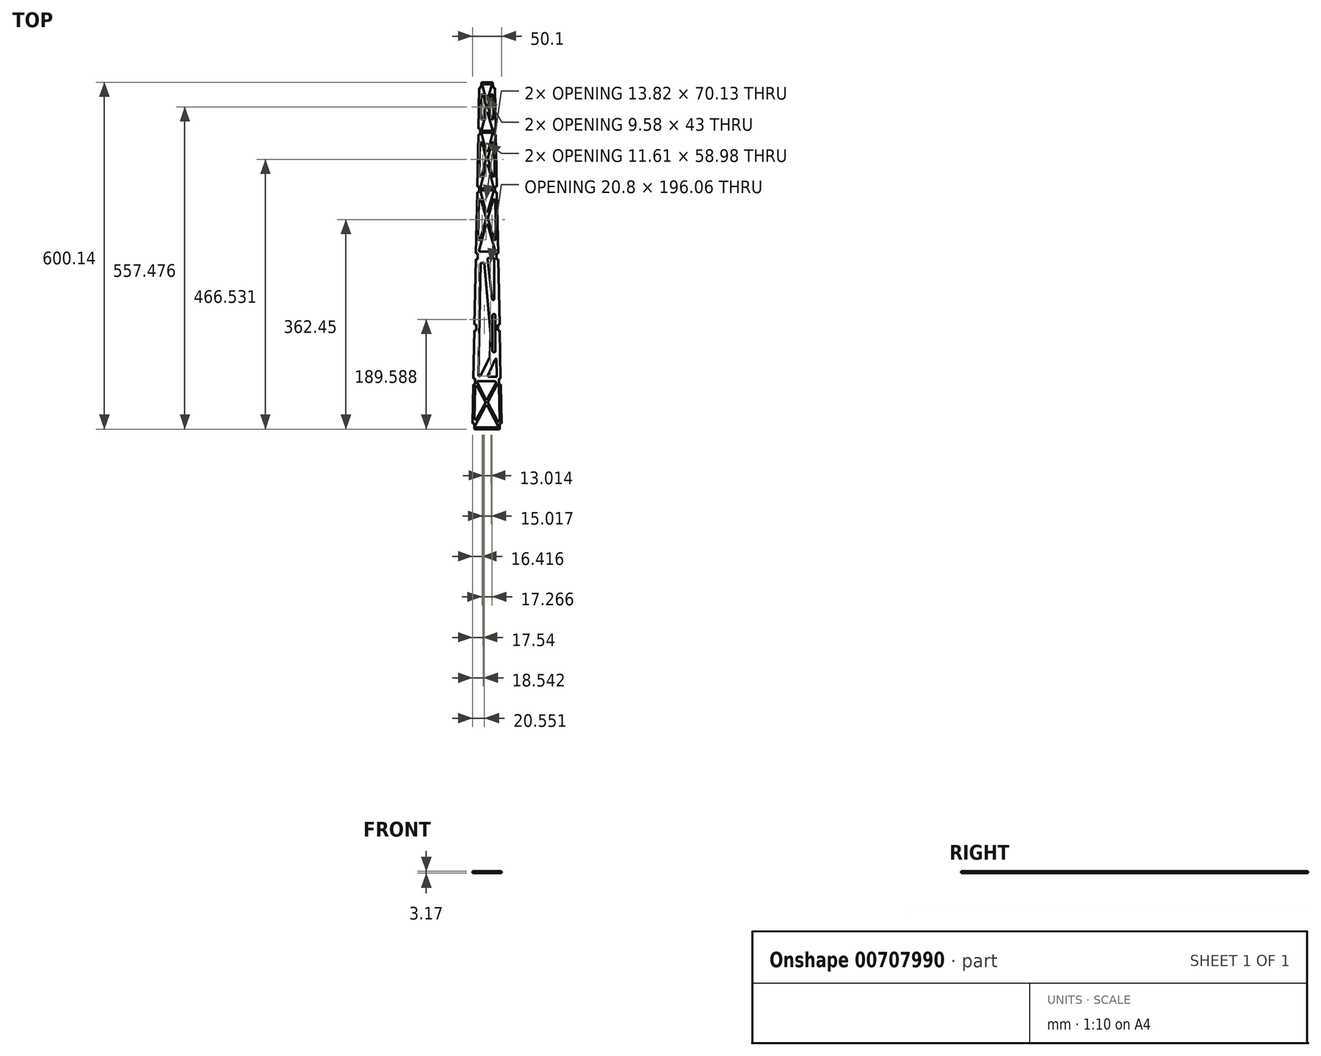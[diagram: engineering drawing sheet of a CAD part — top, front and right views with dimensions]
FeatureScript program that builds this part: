
annotation { "Feature Type Name" : "Feature", "Feature Type Description" : "" }
export const myFeature = defineFeature(function(context is Context, id is Id, definition is map)
    precondition{}
    {
        {
            var Q0;
            Q0=qCreatedBy(makeId("Top.planeOp"), FACE);
            var sketch = newSketch(context, id + "F0", { "sketchPlane" : qUnion([Q0])});
            skLineSegment(sketch, "E0.0.0", {"start": v(-3.6, 283.5) * mm, "end": v(-13.63, 283.5) * mm});
            skLineSegment(sketch, "E1", {"start": v(-14.7, -223.96) * mm, "end": v(1.24, -191.58) * mm});
            skArc(sketch, "E2.filletArc", {"start": v(-18.49, -223.03) * mm, "mid": v(-16.97, -225.02) * mm, "end": v(-14.7, -223.96) * mm});
            skLineSegment(sketch, "E3", {"start": v(1.24, -191.58) * mm, "end": v(2.31, -152.2) * mm});
            skLineSegment(sketch, "E4", {"start": v(2.31, -152.2) * mm, "end": v(-8.41, -29.18) * mm});
            skLineSegment(sketch, "E5.0", {"start": v(18.18, -301.3) * mm, "end": v(17, -241.76) * mm});
            skLineSegment(sketch, "E5.1", {"start": v(11.95, 12.78) * mm, "end": v(10.6, 78.94) * mm});
            skLineSegment(sketch, "E5.2", {"start": v(2.26, 280.33) * mm, "end": v(-9.44, 280.33) * mm});
            skLineSegment(sketch, "E6.0", {"start": v(-14.1, 260.4) * mm, "end": v(-14.89, 221.37) * mm});
            skLineSegment(sketch, "E6.1", {"start": v(-24.24, -244.27) * mm, "end": v(-25.3, -298.14) * mm});
            skLineSegment(sketch, "E6.2", {"start": v(-22.26, -313.46) * mm, "end": v(13.43, -313.46) * mm});
            skLineSegment(sketch, "E7", {"start": v(10.03, -233.97) * mm, "end": v(-18.8, -233.4) * mm});
            skLineSegment(sketch, "E8", {"start": v(8.13, -9.62) * mm, "end": v(-15.31, -9.62) * mm});
            skLineSegment(sketch, "E9", {"start": v(13.25, -240.86) * mm, "end": v(-2.04, -269.42) * mm});
            skLineSegment(sketch, "E10.0", {"start": v(14.42, -302.27) * mm, "end": v(-2.04, -271.3) * mm});
            skLineSegment(sketch, "E11.0", {"start": v(15.2, -310.52) * mm, "end": v(-2.59, -277.05) * mm});
            skLineSegment(sketch, "E12.0", {"start": v(11.75, -236.92) * mm, "end": v(-2.57, -263.67) * mm});
            skLineSegment(sketch, "E13.0", {"start": v(8.02, 12.2) * mm, "end": v(-1.8, 47.72) * mm});
            skLineSegment(sketch, "E14.0", {"start": v(10.06, -7.1) * mm, "end": v(-1.66, 35.3) * mm});
            skLineSegment(sketch, "E15.0", {"start": v(7.42, 94.07) * mm, "end": v(-1.66, 61.2) * mm});
            skLineSegment(sketch, "E16.0", {"start": v(6.68, 79.43) * mm, "end": v(-1.8, 48.78) * mm});
            skLineSegment(sketch, "E17.0", {"start": v(5.78, 121.9) * mm, "end": v(-1.82, 151.59) * mm});
            skLineSegment(sketch, "E18.0", {"start": v(7.53, 102.28) * mm, "end": v(-1.65, 138.11) * mm});
            skLineSegment(sketch, "E19.0", {"start": v(-12.97, 121.9) * mm, "end": v(-5.36, 151.59) * mm});
            skLineSegment(sketch, "E20.0", {"start": v(3.78, 220.81) * mm, "end": v(-1.8, 241.82) * mm});
            skLineSegment(sketch, "E21.MirrorCS", {"start": v(5.45, 202.15) * mm, "end": v(-1.66, 228.88) * mm});
            skLineSegment(sketch, "E22.0", {"start": v(4.2, 277.82) * mm, "end": v(-1.66, 255.8) * mm});
            skLineSegment(sketch, "E23.MirrorCS", {"start": v(2.98, 260.87) * mm, "end": v(-1.8, 242.85) * mm});
            skLineSegment(sketch, "E24.trimOffspring", {"start": v(-5.37, 241.82) * mm, "end": v(-10.96, 220.81) * mm});
            skLineSegment(sketch, "E25.trimOffspring", {"start": v(-5.52, 255.8) * mm, "end": v(-11.38, 277.82) * mm});
            skLineSegment(sketch, "E26.trimOffspring", {"start": v(-5.37, 242.85) * mm, "end": v(-10.16, 260.87) * mm});
            skLineSegment(sketch, "E27.trimOffspring", {"start": v(-5.52, 228.88) * mm, "end": v(-12.63, 202.15) * mm});
            skLineSegment(sketch, "E28.trimOffspring", {"start": v(-5.36, 152.58) * mm, "end": v(-11.85, 177.9) * mm});
            skLineSegment(sketch, "E29.trimOffspring", {"start": v(-1.82, 152.58) * mm, "end": v(4.66, 177.9) * mm});
            skLineSegment(sketch, "E30.trimOffspring", {"start": v(-5.53, 166.05) * mm, "end": v(-12.68, 193.96) * mm});
            skLineSegment(sketch, "E31.trimOffspring", {"start": v(-1.65, 166.05) * mm, "end": v(5.5, 193.96) * mm});
            skLineSegment(sketch, "E32.trimOffspring", {"start": v(-5.39, 48.78) * mm, "end": v(-13.86, 79.43) * mm});
            skLineSegment(sketch, "E33.trimOffspring", {"start": v(-5.52, 35.3) * mm, "end": v(-17.24, -7.1) * mm});
            skLineSegment(sketch, "E34.trimOffspring", {"start": v(-5.52, 61.2) * mm, "end": v(-14.6, 94.07) * mm});
            skLineSegment(sketch, "E35.trimOffspring", {"start": v(-5.39, 47.72) * mm, "end": v(-15.2, 12.2) * mm});
            skLineSegment(sketch, "E36.trimOffspring", {"start": v(-6.64, -269.41) * mm, "end": v(-20.48, -243.37) * mm});
            skLineSegment(sketch, "E37.trimOffspring", {"start": v(-6.65, -271.3) * mm, "end": v(-21.54, -299.12) * mm});
            skLineSegment(sketch, "E38.trimOffspring", {"start": v(-6.1, -263.66) * mm, "end": v(-20.6, -236.34) * mm});
            skLineSegment(sketch, "E39.trimOffspring", {"start": v(-6.12, -277.04) * mm, "end": v(-24.03, -310.51) * mm});
            skLineSegment(sketch, "E40.trimOffspring", {"start": v(9.72, 122.43) * mm, "end": v(8.6, 177.45) * mm});
            skLineSegment(sketch, "E41.trimOffspring", {"start": v(-17.79, 78.94) * mm, "end": v(-19.13, 12.78) * mm});
            skLineSegment(sketch, "E42.trimOffspring", {"start": v(-15.78, 177.45) * mm, "end": v(-16.9, 122.43) * mm});
            skLineSegment(sketch, "E43.trimOffspring", {"start": v(7.7, 221.37) * mm, "end": v(6.91, 260.4) * mm});
            skLineSegment(sketch, "E44", {"start": v(10.22, -197.1) * mm, "end": v(-1.88, -223.48) * mm});
            skLineSegment(sketch, "E45", {"start": v(-0.06, -226.3) * mm, "end": v(11.28, -226.3) * mm});
            skLineSegment(sketch, "E46", {"start": v(13.28, -224.27) * mm, "end": v(12.72, -195.53) * mm});
            skLineSegment(sketch, "E47", {"start": v(11.16, -195.18) * mm, "end": v(10.22, -197.1) * mm});
            skLineSegment(sketch, "E48", {"start": v(6.99, -20.51) * mm, "end": v(-0.88, -20.67) * mm});
            skLineSegment(sketch, "E49", {"start": v(-2.83, -22.9) * mm, "end": v(5.04, -91.54) * mm});
            skLineSegment(sketch, "E50", {"start": v(9.03, -91.32) * mm, "end": v(9.03, -22.51) * mm});
            skPoint(sketch, "E51.visualSharp", {"position": v(16.76, -313.46) * mm});
            skArc(sketch, "E51.filletArc", {"start": v(13.43, -313.46) * mm, "mid": v(15.14, -312.49) * mm, "end": v(15.2, -310.52) * mm});
            skArc(sketch, "E52.filletArc", {"start": v(14.42, -302.27) * mm, "mid": v(16.68, -303.27) * mm, "end": v(18.18, -301.3) * mm});
            skArc(sketch, "E53.filletArc", {"start": v(17, -241.76) * mm, "mid": v(15.48, -239.86) * mm, "end": v(13.25, -240.86) * mm});
            skArc(sketch, "E54.filletArc", {"start": v(-20.48, -243.37) * mm, "mid": v(-22.7, -242.37) * mm, "end": v(-24.24, -244.27) * mm});
            skArc(sketch, "E55.filletArc", {"start": v(-25.3, -298.14) * mm, "mid": v(-23.8, -300.11) * mm, "end": v(-21.54, -299.12) * mm});
            skArc(sketch, "E56.filletArc", {"start": v(-24.03, -310.51) * mm, "mid": v(-23.98, -312.49) * mm, "end": v(-22.26, -313.46) * mm});
            skPoint(sketch, "E57.visualSharp", {"position": v(-22.2, -233.34) * mm});
            skArc(sketch, "E57.filletArc", {"start": v(-18.8, -233.4) * mm, "mid": v(-20.55, -234.36) * mm, "end": v(-20.6, -236.34) * mm});
            skPoint(sketch, "E58.visualSharp", {"position": v(13.29, -234.04) * mm});
            skArc(sketch, "E58.filletArc", {"start": v(11.75, -236.92) * mm, "mid": v(11.71, -234.96) * mm, "end": v(10.03, -233.97) * mm});
            skPoint(sketch, "E59.visualSharp", {"position": v(-4.34, -266.98) * mm});
            skArc(sketch, "E59.filletArc", {"start": v(-6.1, -263.66) * mm, "mid": v(-4.33, -264.72) * mm, "end": v(-2.57, -263.67) * mm});
            skPoint(sketch, "E60.visualSharp", {"position": v(-6.14, -270.35) * mm});
            skArc(sketch, "E60.filletArc", {"start": v(-6.65, -271.3) * mm, "mid": v(-6.4, -270.35) * mm, "end": v(-6.64, -269.41) * mm});
            skPoint(sketch, "E61.visualSharp", {"position": v(-4.35, -273.73) * mm});
            skArc(sketch, "E61.filletArc", {"start": v(-2.59, -277.05) * mm, "mid": v(-4.35, -275.99) * mm, "end": v(-6.12, -277.04) * mm});
            skPoint(sketch, "E62.visualSharp", {"position": v(-2.54, -270.36) * mm});
            skArc(sketch, "E62.filletArc", {"start": v(-2.04, -269.42) * mm, "mid": v(-2.27, -270.36) * mm, "end": v(-2.04, -271.3) * mm});
            skPoint(sketch, "E63.visualSharp", {"position": v(-3.18, -226.3) * mm});
            skArc(sketch, "E63.filletArc", {"start": v(-1.88, -223.48) * mm, "mid": v(-1.75, -225.39) * mm, "end": v(-0.06, -226.3) * mm});
            skPoint(sketch, "E64.visualSharp", {"position": v(13.32, -226.3) * mm});
            skArc(sketch, "E64.filletArc", {"start": v(11.28, -226.3) * mm, "mid": v(12.7, -225.71) * mm, "end": v(13.28, -224.27) * mm});
            skPoint(sketch, "E65.visualSharp", {"position": v(12.65, -192.14) * mm});
            skArc(sketch, "E65.filletArc", {"start": v(12.72, -195.53) * mm, "mid": v(12.07, -194.74) * mm, "end": v(11.16, -195.18) * mm});
            skPoint(sketch, "E66.visualSharp", {"position": v(9.03, -126.31) * mm});
            skPoint(sketch, "E67.visualSharp", {"position": v(9.03, -20.47) * mm});
            skArc(sketch, "E67.filletArc", {"start": v(9.03, -22.51) * mm, "mid": v(8.43, -21.09) * mm, "end": v(6.99, -20.51) * mm});
            skPoint(sketch, "E68.visualSharp", {"position": v(-3.08, -20.72) * mm});
            skArc(sketch, "E68.filletArc", {"start": v(-0.88, -20.67) * mm, "mid": v(-2.35, -21.36) * mm, "end": v(-2.83, -22.9) * mm});
            skArc(sketch, "E69.filletArc", {"start": v(8.02, 12.2) * mm, "mid": v(10.24, 10.76) * mm, "end": v(11.95, 12.78) * mm});
            skPoint(sketch, "E70.visualSharp", {"position": v(10.76, -9.62) * mm});
            skArc(sketch, "E70.filletArc", {"start": v(8.13, -9.62) * mm, "mid": v(9.72, -8.83) * mm, "end": v(10.06, -7.1) * mm});
            skPoint(sketch, "E71.visualSharp", {"position": v(-17.94, -9.62) * mm});
            skArc(sketch, "E71.filletArc", {"start": v(-17.24, -7.1) * mm, "mid": v(-16.9, -8.83) * mm, "end": v(-15.31, -9.62) * mm});
            skArc(sketch, "E72.filletArc", {"start": v(-19.13, 12.78) * mm, "mid": v(-17.42, 10.76) * mm, "end": v(-15.2, 12.2) * mm});
            skArc(sketch, "E73.filletArc", {"start": v(-13.86, 79.43) * mm, "mid": v(-16.04, 80.89) * mm, "end": v(-17.79, 78.94) * mm});
            skPoint(sketch, "E74.visualSharp", {"position": v(-3.6, 54.22) * mm});
            skArc(sketch, "E74.filletArc", {"start": v(-5.52, 61.2) * mm, "mid": v(-3.6, 59.73) * mm, "end": v(-1.66, 61.2) * mm});
            skPoint(sketch, "E75.visualSharp", {"position": v(-1.94, 48.25) * mm});
            skArc(sketch, "E75.filletArc", {"start": v(-1.8, 48.78) * mm, "mid": v(-1.87, 48.25) * mm, "end": v(-1.8, 47.72) * mm});
            skPoint(sketch, "E76.visualSharp", {"position": v(-3.6, 42.28) * mm});
            skArc(sketch, "E76.filletArc", {"start": v(-1.66, 35.3) * mm, "mid": v(-3.6, 36.78) * mm, "end": v(-5.52, 35.3) * mm});
            skPoint(sketch, "E77.visualSharp", {"position": v(-5.24, 48.25) * mm});
            skArc(sketch, "E77.filletArc", {"start": v(-5.39, 47.72) * mm, "mid": v(-5.32, 48.25) * mm, "end": v(-5.39, 48.78) * mm});
            skArc(sketch, "E78.filletArc", {"start": v(10.6, 78.94) * mm, "mid": v(8.85, 80.89) * mm, "end": v(6.68, 79.43) * mm});
            skLineSegment(sketch, "E79.0", {"start": v(5.59, 99.78) * mm, "end": v(-12.77, 99.78) * mm});
            skLineSegment(sketch, "E80.MirrorCS", {"start": v(5.5, 96.6) * mm, "end": v(-12.68, 96.6) * mm});
            skLineSegment(sketch, "E81.0", {"start": v(3.51, 199.63) * mm, "end": v(-10.7, 199.63) * mm});
            skLineSegment(sketch, "E82.MirrorCS", {"start": v(3.56, 196.45) * mm, "end": v(-10.74, 196.45) * mm});
            skLineSegment(sketch, "E83.trimOffspring", {"start": v(-14.7, 102.28) * mm, "end": v(-5.53, 138.11) * mm});
            skArc(sketch, "E84.filletArc", {"start": v(7.42, 94.07) * mm, "mid": v(7.09, 95.81) * mm, "end": v(5.5, 96.6) * mm});
            skArc(sketch, "E85.filletArc", {"start": v(-12.68, 96.6) * mm, "mid": v(-14.27, 95.81) * mm, "end": v(-14.6, 94.07) * mm});
            skArc(sketch, "E86.filletArc", {"start": v(-14.7, 102.28) * mm, "mid": v(-14.35, 100.56) * mm, "end": v(-12.77, 99.78) * mm});
            skArc(sketch, "E87.filletArc", {"start": v(5.59, 99.78) * mm, "mid": v(7.17, 100.56) * mm, "end": v(7.53, 102.28) * mm});
            skArc(sketch, "E88.filletArc", {"start": v(5.78, 121.9) * mm, "mid": v(8, 120.4) * mm, "end": v(9.72, 122.43) * mm});
            skArc(sketch, "E89.filletArc", {"start": v(-16.9, 122.43) * mm, "mid": v(-15.17, 120.4) * mm, "end": v(-12.97, 121.9) * mm});
            skArc(sketch, "E90.filletArc", {"start": v(5.5, 193.96) * mm, "mid": v(5.14, 195.68) * mm, "end": v(3.56, 196.45) * mm});
            skArc(sketch, "E91.filletArc", {"start": v(3.51, 199.63) * mm, "mid": v(5.1, 200.41) * mm, "end": v(5.45, 202.15) * mm});
            skArc(sketch, "E92.filletArc", {"start": v(-12.63, 202.15) * mm, "mid": v(-12.28, 200.41) * mm, "end": v(-10.7, 199.63) * mm});
            skArc(sketch, "E93.filletArc", {"start": v(-10.74, 196.45) * mm, "mid": v(-12.32, 195.68) * mm, "end": v(-12.68, 193.96) * mm});
            skPoint(sketch, "E94.visualSharp", {"position": v(-3.6, 236.15) * mm});
            skArc(sketch, "E94.filletArc", {"start": v(-1.66, 228.88) * mm, "mid": v(-3.6, 230.36) * mm, "end": v(-5.52, 228.88) * mm});
            skPoint(sketch, "E95.visualSharp", {"position": v(-3.6, 158.5) * mm});
            skArc(sketch, "E95.filletArc", {"start": v(-5.53, 166.05) * mm, "mid": v(-3.6, 164.55) * mm, "end": v(-1.65, 166.05) * mm});
            skPoint(sketch, "E96.visualSharp", {"position": v(-3.6, 248.53) * mm});
            skArc(sketch, "E96.filletArc", {"start": v(-5.52, 255.8) * mm, "mid": v(-3.6, 254.31) * mm, "end": v(-1.66, 255.8) * mm});
            skPoint(sketch, "E97.visualSharp", {"position": v(-12.05, 280.33) * mm});
            skArc(sketch, "E97.filletArc", {"start": v(-9.44, 280.33) * mm, "mid": v(-11.03, 279.55) * mm, "end": v(-11.38, 277.82) * mm});
            skArc(sketch, "E98.filletArc", {"start": v(4.2, 277.82) * mm, "mid": v(3.85, 279.55) * mm, "end": v(2.26, 280.33) * mm});
            skPoint(sketch, "E99.visualSharp", {"position": v(-5.24, 242.34) * mm});
            skArc(sketch, "E99.filletArc", {"start": v(-5.37, 241.82) * mm, "mid": v(-5.3, 242.34) * mm, "end": v(-5.37, 242.85) * mm});
            skPoint(sketch, "E100.visualSharp", {"position": v(-1.95, 242.34) * mm});
            skArc(sketch, "E100.filletArc", {"start": v(-1.8, 242.85) * mm, "mid": v(-1.88, 242.34) * mm, "end": v(-1.8, 241.82) * mm});
            skArc(sketch, "E101.filletArc", {"start": v(8.6, 177.45) * mm, "mid": v(6.83, 179.4) * mm, "end": v(4.66, 177.9) * mm});
            skArc(sketch, "E102.filletArc", {"start": v(-11.85, 177.9) * mm, "mid": v(-14.01, 179.4) * mm, "end": v(-15.78, 177.45) * mm});
            skArc(sketch, "E103.filletArc", {"start": v(-14.89, 221.37) * mm, "mid": v(-13.17, 219.35) * mm, "end": v(-10.96, 220.81) * mm});
            skArc(sketch, "E104.filletArc", {"start": v(-10.16, 260.87) * mm, "mid": v(-12.34, 262.35) * mm, "end": v(-14.1, 260.4) * mm});
            skArc(sketch, "E105.filletArc", {"start": v(6.91, 260.4) * mm, "mid": v(5.15, 262.35) * mm, "end": v(2.98, 260.87) * mm});
            skArc(sketch, "E106.filletArc", {"start": v(3.78, 220.81) * mm, "mid": v(5.99, 219.35) * mm, "end": v(7.7, 221.37) * mm});
            skPoint(sketch, "E107.visualSharp", {"position": v(-3.6, 145.68) * mm});
            skArc(sketch, "E107.filletArc", {"start": v(-1.65, 138.11) * mm, "mid": v(-3.6, 139.62) * mm, "end": v(-5.53, 138.11) * mm});
            skPoint(sketch, "E108.visualSharp", {"position": v(-5.23, 152.08) * mm});
            skArc(sketch, "E108.filletArc", {"start": v(-5.36, 151.59) * mm, "mid": v(-5.3, 152.08) * mm, "end": v(-5.36, 152.58) * mm});
            skPoint(sketch, "E109.visualSharp", {"position": v(-1.95, 152.08) * mm});
            skArc(sketch, "E109.filletArc", {"start": v(-1.82, 152.58) * mm, "mid": v(-1.89, 152.08) * mm, "end": v(-1.82, 151.59) * mm});
            skArc(sketch, "E110.filletArc", {"start": v(5.04, -91.54) * mm, "mid": v(7.14, -93.31) * mm, "end": v(9.03, -91.32) * mm});
            skLineSegment(sketch, "E111", {"start": v(-18.49, -223.03) * mm, "end": v(-14.63, -29.01) * mm});
            skLineSegment(sketch, "E112", {"start": v(8.43, -120.01) * mm, "end": v(8.43, -181.2) * mm, "construction": true});
            skArc(sketch, "E113.0.startCap", {"start": v(5.93, -120.01) * mm, "mid": v(8.43, -117.51) * mm, "end": v(10.93, -120.01) * mm});
            skArc(sketch, "E113.0.endCap", {"start": v(10.93, -181.2) * mm, "mid": v(8.43, -183.7) * mm, "end": v(5.93, -181.2) * mm});
            skLineSegment(sketch, "E113.0.left", {"start": v(10.93, -120.01) * mm, "end": v(10.93, -181.2) * mm});
            skLineSegment(sketch, "E113.0.right", {"start": v(5.93, -120.01) * mm, "end": v(5.93, -181.2) * mm});
            skLineSegment(sketch, "E114.bottom", {"start": v(-27.12, -229.08) * mm, "end": v(-23.94, -229.14) * mm});
            skLineSegment(sketch, "E114.top", {"start": v(-27.31, -239.08) * mm, "end": v(-24.14, -239.14) * mm});
            skLineSegment(sketch, "E114.right", {"start": v(-23.94, -229.14) * mm, "end": v(-24.14, -239.14) * mm});
            skLineSegment(sketch, "E115", {"start": v(-4.39, -233.69) * mm, "end": v(-4.71, -315.99) * mm, "construction": true});
            skLineSegment(sketch, "E116.bottom", {"start": v(-25.28, -135.92) * mm, "end": v(-22.11, -135.98) * mm});
            skLineSegment(sketch, "E116.top", {"start": v(-25.48, -145.92) * mm, "end": v(-22.3, -145.98) * mm});
            skLineSegment(sketch, "E117.trimOffspring", {"start": v(-25.48, -145.92) * mm, "end": v(-27.12, -229.08) * mm});
            skLineSegment(sketch, "E118.bottom", {"start": v(-22.83, -12.78) * mm, "end": v(-19.66, -12.84) * mm});
            skLineSegment(sketch, "E118.top", {"start": v(-23.03, -22.78) * mm, "end": v(-19.86, -22.84) * mm});
            skLineSegment(sketch, "E118.right", {"start": v(-19.66, -12.84) * mm, "end": v(-19.86, -22.84) * mm});
            skLineSegment(sketch, "E119.bottom", {"start": v(-20.47, 103.2) * mm, "end": v(-17.3, 103.14) * mm});
            skLineSegment(sketch, "E119.top", {"start": v(-20.67, 93.2) * mm, "end": v(-17.5, 93.14) * mm});
            skLineSegment(sketch, "E119.right", {"start": v(-17.3, 103.14) * mm, "end": v(-17.5, 93.14) * mm});
            skLineSegment(sketch, "E120.trimOffspring", {"start": v(-20.67, 93.2) * mm, "end": v(-22.83, -12.78) * mm});
            skLineSegment(sketch, "E121.bottom", {"start": v(-18.44, 203.35) * mm, "end": v(-15.26, 203.29) * mm});
            skLineSegment(sketch, "E121.top", {"start": v(-18.64, 193.35) * mm, "end": v(-15.46, 193.3) * mm});
            skLineSegment(sketch, "E121.right", {"start": v(-15.26, 203.29) * mm, "end": v(-15.46, 193.3) * mm});
            skLineSegment(sketch, "E122.trimOffspring", {"start": v(-18.64, 193.35) * mm, "end": v(-20.47, 103.2) * mm});
            skLineSegment(sketch, "E123.top", {"start": v(-17, 273.51) * mm, "end": v(-13.82, 273.45) * mm});
            skLineSegment(sketch, "E124", {"start": v(-17, 273.51) * mm, "end": v(-18.44, 203.35) * mm});
            skLineSegment(sketch, "E125", {"start": v(-25.67, -316.63) * mm, "end": v(-4.71, -316.63) * mm});
            skLineSegment(sketch, "E126", {"start": v(-4.71, -315.99) * mm, "end": v(-4.71, -321.59) * mm, "construction": true});
            skLineSegment(sketch, "E127", {"start": v(-3.6, 283.5) * mm, "end": v(-3.6, 292.07) * mm, "construction": true});
            skLineSegment(sketch, "E128", {"start": v(-23.03, -22.78) * mm, "end": v(-25.28, -135.92) * mm});
            skLineSegment(sketch, "E129", {"start": v(-25.47, -306.6) * mm, "end": v(-25.67, -316.63) * mm});
            skLineSegment(sketch, "E130.MirrorCS", {"start": v(-3.6, 283.5) * mm, "end": v(6.44, 283.5) * mm});
            skLineSegment(sketch, "E131.MirrorCS", {"start": v(9.82, 273.51) * mm, "end": v(6.64, 273.45) * mm});
            skLineSegment(sketch, "E132.MirrorCS", {"start": v(9.82, 273.51) * mm, "end": v(11.26, 203.35) * mm});
            skLineSegment(sketch, "E133.MirrorCS", {"start": v(11.26, 203.35) * mm, "end": v(8.08, 203.29) * mm});
            skLineSegment(sketch, "E134.MirrorCS", {"start": v(8.08, 203.29) * mm, "end": v(8.28, 193.3) * mm});
            skLineSegment(sketch, "E135.MirrorCS", {"start": v(11.45, 193.35) * mm, "end": v(8.28, 193.3) * mm});
            skLineSegment(sketch, "E136.MirrorCS", {"start": v(11.45, 193.35) * mm, "end": v(13.29, 103.2) * mm});
            skLineSegment(sketch, "E137.MirrorCS", {"start": v(13.29, 103.2) * mm, "end": v(10.12, 103.14) * mm});
            skLineSegment(sketch, "E138.MirrorCS", {"start": v(10.12, 103.14) * mm, "end": v(10.32, 93.14) * mm});
            skLineSegment(sketch, "E139.MirrorCS", {"start": v(13.5, 93.2) * mm, "end": v(10.32, 93.14) * mm});
            skLineSegment(sketch, "E140.MirrorCS", {"start": v(13.5, 93.2) * mm, "end": v(15.65, -12.78) * mm});
            skLineSegment(sketch, "E141.MirrorCS", {"start": v(15.65, -12.78) * mm, "end": v(12.48, -12.84) * mm});
            skLineSegment(sketch, "E142.MirrorCS", {"start": v(12.48, -12.84) * mm, "end": v(12.68, -22.84) * mm});
            skLineSegment(sketch, "E143.MirrorCS", {"start": v(15.85, -22.78) * mm, "end": v(12.68, -22.84) * mm});
            skLineSegment(sketch, "E144.MirrorCS", {"start": v(15.85, -22.78) * mm, "end": v(18.1, -135.92) * mm});
            skLineSegment(sketch, "E145.MirrorCS", {"start": v(18.1, -135.92) * mm, "end": v(14.93, -135.98) * mm});
            skLineSegment(sketch, "E146.MirrorCS", {"start": v(18.3, -145.92) * mm, "end": v(15.12, -145.98) * mm});
            skLineSegment(sketch, "E147.MirrorCS", {"start": v(18.3, -145.92) * mm, "end": v(19.94, -229.08) * mm});
            skLineSegment(sketch, "E148.MirrorCS", {"start": v(19.94, -229.08) * mm, "end": v(16.76, -229.14) * mm});
            skLineSegment(sketch, "E149.MirrorCS", {"start": v(16.76, -229.14) * mm, "end": v(16.96, -239.14) * mm});
            skLineSegment(sketch, "E150.MirrorCS", {"start": v(20.13, -239.08) * mm, "end": v(16.96, -239.14) * mm});
            skLineSegment(sketch, "E151.MirrorCS", {"start": v(20.13, -239.08) * mm, "end": v(21.46, -306.54) * mm});
            skLineSegment(sketch, "E152.MirrorCS", {"start": v(18.29, -306.6) * mm, "end": v(21.46, -306.54) * mm});
            skLineSegment(sketch, "E153.MirrorCS", {"start": v(18.29, -306.6) * mm, "end": v(18.48, -316.63) * mm});
            skLineSegment(sketch, "E154", {"start": v(-4.71, -316.63) * mm, "end": v(18.48, -316.63) * mm});
            skLineSegment(sketch, "E155", {"start": v(14.93, -135.98) * mm, "end": v(15.12, -145.98) * mm});
            skLineSegment(sketch, "E156", {"start": v(-22.11, -135.98) * mm, "end": v(-22.3, -145.98) * mm});
            skLineSegment(sketch, "E157", {"start": v(-8.41, -29.18) * mm, "end": v(-14.63, -29.01) * mm});
            skPoint(sketch, "E158.trimOffspring.end.orphan", {"position": v(-28.64, -306.54) * mm});
            skLineSegment(sketch, "E159", {"start": v(-27.31, -239.08) * mm, "end": v(-28.64, -306.54) * mm});
            skLineSegment(sketch, "E160", {"start": v(-25.47, -306.6) * mm, "end": v(-28.64, -306.54) * mm});
            skLineSegment(sketch, "E161", {"start": v(-13.63, 283.5) * mm, "end": v(-13.82, 273.45) * mm});
            skLineSegment(sketch, "E162", {"start": v(6.44, 283.5) * mm, "end": v(6.64, 273.45) * mm});
            skSolve(sketch);
        }
        {
            var Q0;
            Q0 = qSketchRegion(id + "F0", true);
            extrude(context, id + "F1", {"entities" : qUnion([Q0]), "depth" : 3.17 * mm, "offsetDistance" : 25 * mm});
        }
    });
